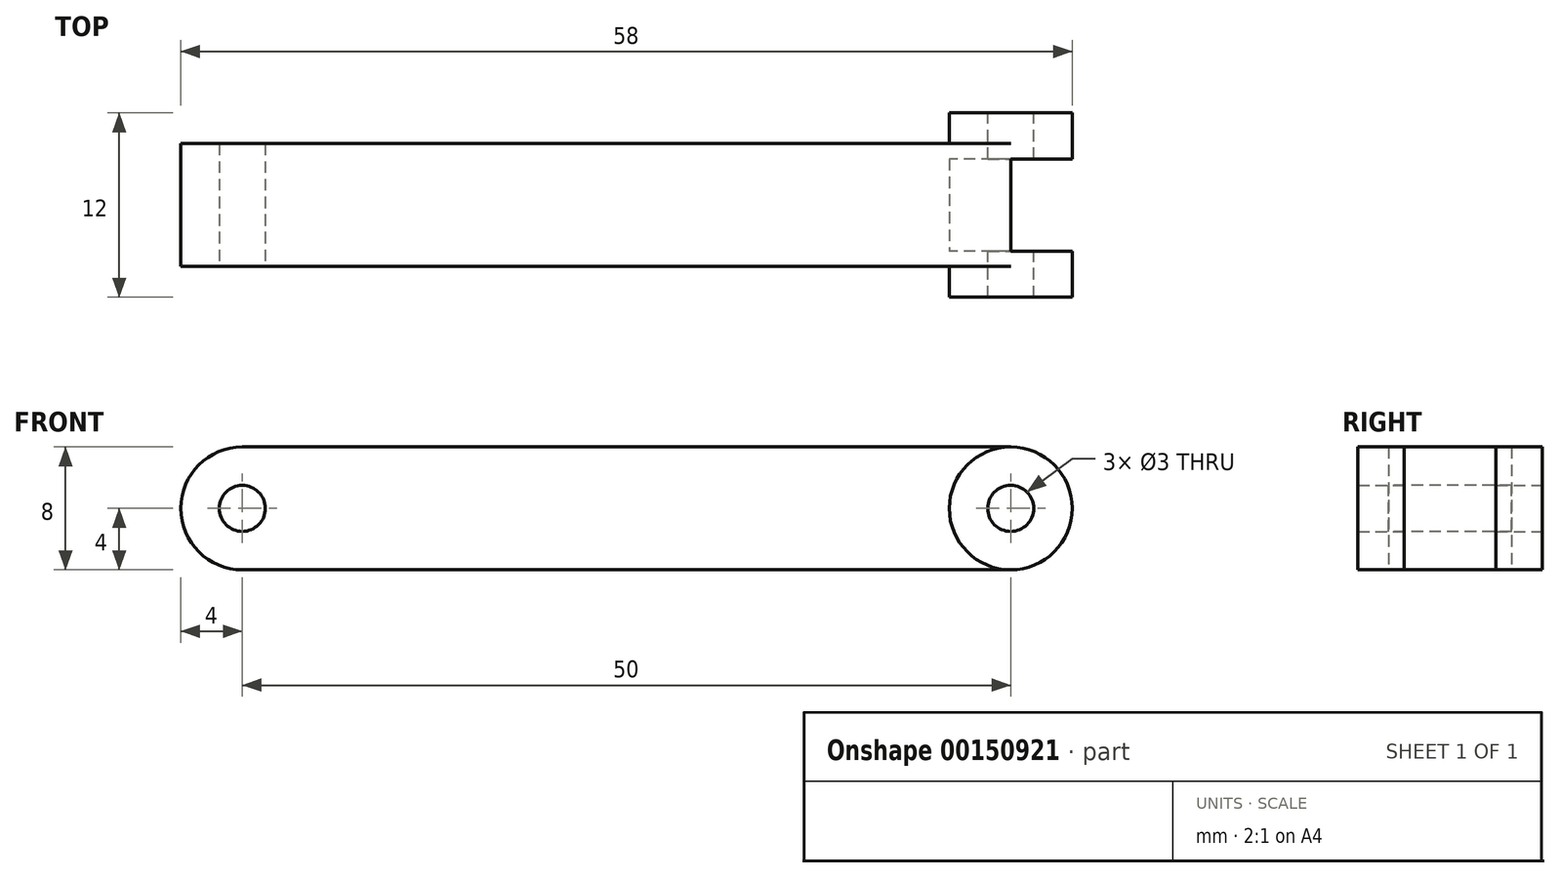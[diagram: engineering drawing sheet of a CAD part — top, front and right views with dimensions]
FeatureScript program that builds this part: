
annotation { "Feature Type Name" : "Feature", "Feature Type Description" : "" }
export const myFeature = defineFeature(function(context is Context, id is Id, definition is map)
    precondition{}
    {
        {
            var Q0;
            Q0=qCreatedBy(makeId("Front.planeOp"),FACE);
            var sketch = newSketch(context, id + "F0", { "sketchPlane" : qUnion([Q0])});
            skLineSegment(sketch, "E0.bottom", {"start": v(0, 0) * mm, "end": v(50, 0) * mm});
            skLineSegment(sketch, "E0.top", {"start": v(0, 8) * mm, "end": v(50, 8) * mm});
            skArc(sketch, "E1", {"start": v(0, 8) * mm, "mid": v(-4, 4) * mm, "end": v(0, 0) * mm});
            skArc(sketch, "E2", {"start": v(50, 0) * mm, "mid": v(54, 4) * mm, "end": v(50, 8) * mm});
            skSolve(sketch);
        }
        {
            var Q0;
            Q0=qSketchRegion(id+"F0",true);
            extrude(context, id + "F1", {"entities" : qUnion([Q0]), "endBound" : BoundingType.SYMMETRIC, "depth" : 8 * mm});
        }
        {
            var Q0;
            Q0=makeQuery(id+"F1.opExtrude","CAP_FACE",FACE,{"disambiguationData":[OSD([sQuery(id+"F0.wireOp",EDGE,"E0.bottom"),sQuery(id+"F0.wireOp",EDGE,"E0.top"),sQuery(id+"F0.wireOp",EDGE,"HIoaqUXj-zCnZ-PLay-zYgn-YaQb4ij7V86C"),sQuery(id+"F0.wireOp",EDGE,"LPRup51T-Z1iP-anKY-cxDH-ksB0blUbg6ey")])],"isStart":false});
            var sketch = newSketch(context, id + "F2", { "sketchPlane" : qUnion([Q0])});
            skCircle(sketch, "E3", {"center": v(0, 4) * mm, "radius": 1.5 * mm});
            skSolve(sketch);
        }
        {
            var Q0;
            Q0=qSketchRegion(id+"F2",true);
            extrude(context, id + "F3", {"entities" : qUnion([Q0]), "operationType" : NewBodyOperationType.REMOVE, "endBound" : BoundingType.THROUGH_ALL, "oppositeDirection" : true, "depth" : 25 * mm});
        }
        {
            var Q0;
            Q0=makeQuery(id+"F1.opExtrude","CAP_FACE",FACE,{"disambiguationData":[OSD([sQuery(id+"F0.wireOp",EDGE,"E0.bottom"),sQuery(id+"F0.wireOp",EDGE,"E0.top"),sQuery(id+"F0.wireOp",EDGE,"HIoaqUXj-zCnZ-PLay-zYgn-YaQb4ij7V86C"),sQuery(id+"F0.wireOp",EDGE,"LPRup51T-Z1iP-anKY-cxDH-ksB0blUbg6ey")])],"isStart":false});
            var sketch = newSketch(context, id + "F4", { "sketchPlane" : qUnion([Q0])});
            skCircle(sketch, "E4", {"center": v(50, 4) * mm, "radius": 1.5 * mm});
            skSolve(sketch);
        }
        {
            var Q0;
            Q0=qCreatedBy(makeId("Front.planeOp"),FACE);
            var sketch = newSketch(context, id + "F5", { "sketchPlane" : qUnion([Q0])});
            skCircle(sketch, "E5", {"center": v(50, 4) * mm, "radius": 4 * mm});
            skSolve(sketch);
        }
        {
            var Q0;
            Q0 = qSketchRegion(id + "F5", true);
            extrude(context, id + "F6", {"entities" : qUnion([Q0]), "operationType" : NewBodyOperationType.ADD, "endBound" : BoundingType.SYMMETRIC, "oppositeDirection" : true, "depth" : 12 * mm});
        }
        {
            var Q0;
            Q0=qCreatedBy(makeId("Front.planeOp"),FACE);
            var sketch = newSketch(context, id + "F7", { "sketchPlane" : qUnion([Q0])});
            skCircle(sketch, "E6", {"center": v(50, 4) * mm, "radius": 4 * mm});
            skSolve(sketch);
        }
        {
            var Q0;
            Q0 = qSketchRegion(id + "F7", true);
            extrude(context, id + "F8", {"entities" : qUnion([Q0]), "operationType" : NewBodyOperationType.REMOVE, "endBound" : BoundingType.SYMMETRIC, "oppositeDirection" : true, "depth" : 6 * mm});
        }
        {
            var Q0;
            Q0 = qSketchRegion(id + "F4", true);
            extrude(context, id + "F9", {"entities" : qUnion([Q0]), "operationType" : NewBodyOperationType.REMOVE, "endBound" : BoundingType.SYMMETRIC, "depth" : 25 * mm});
        }
    });
